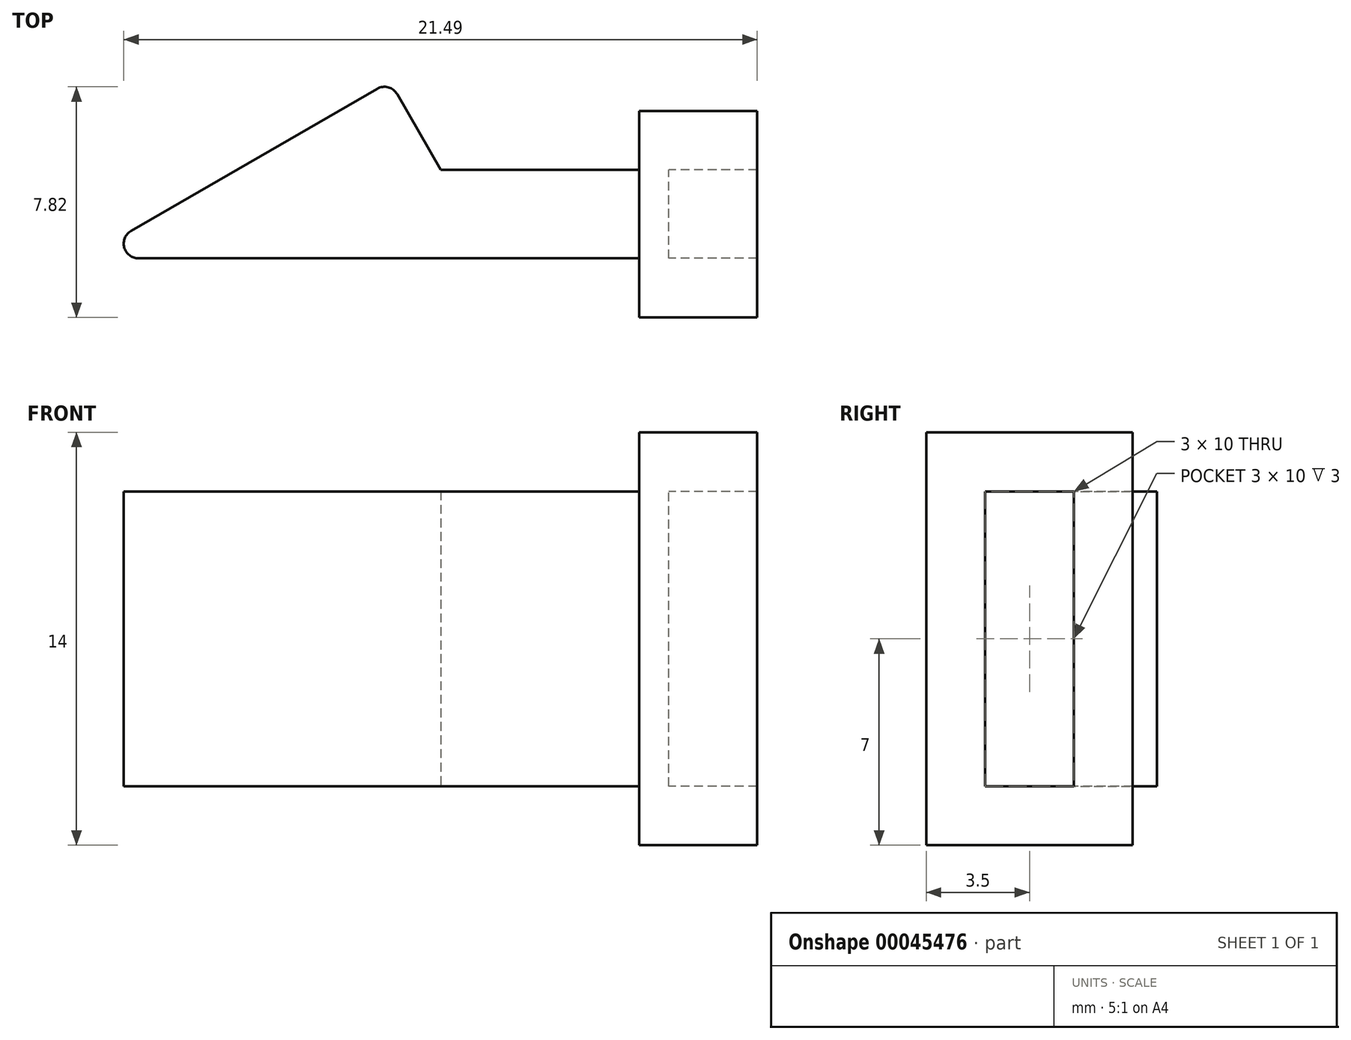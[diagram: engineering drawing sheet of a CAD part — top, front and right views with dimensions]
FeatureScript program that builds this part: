
annotation { "Feature Type Name" : "Feature", "Feature Type Description" : "" }
export const myFeature = defineFeature(function(context is Context, id is Id, definition is map)
    precondition{}
    {
        {
            var Q0;
            Q0=qCreatedBy(makeId("Top.planeOp"),FACE);
            var sketch = newSketch(context, id + "F0", { "sketchPlane" : qUnion([Q0])});
            skLineSegment(sketch, "E0", {"start": v(0, 0) * mm, "end": v(-13.86, 0) * mm});
            skLineSegment(sketch, "E1", {"start": v(-13.86, 0) * mm, "end": v(-3.46, 6) * mm});
            skLineSegment(sketch, "E2", {"start": v(-3.46, 6) * mm, "end": v(0, 0) * mm});
            skLineSegment(sketch, "E3", {"start": v(-3.46, 6) * mm, "end": v(-3.46, 0) * mm, "construction": true});
            skSolve(sketch);
        }
        {
            var Q0;
            Q0=qSketchRegion(id+"F0",true);
            extrude(context, id + "F1", {"entities" : qUnion([Q0]), "depth" : 10 * mm});
        }
        {
            var Q0;
            Q0=qCreatedBy(makeId("Right.planeOp"),FACE);
            cPlane(context, id + "F2", {"entities" : qUnion([Q0]), "cplaneType" : CPlaneType.OFFSET, "offset" : 3.46 * mm, "oppositeDirection" : true, "width" : 150 * mm, "height" : 150 * mm});
        }
        {
            var Q0;
            Q0=qCreatedBy(id+"F2.planeOp",FACE);
            var sketch = newSketch(context, id + "F3", { "sketchPlane" : qUnion([Q0])});
            skLineSegment(sketch, "E4.bottom", {"start": v(0, 0) * mm, "end": v(3, 0) * mm});
            skLineSegment(sketch, "E4.top", {"start": v(0, 10) * mm, "end": v(3, 10) * mm});
            skLineSegment(sketch, "E4.left", {"start": v(0, 0) * mm, "end": v(0, 10) * mm});
            skLineSegment(sketch, "E4.right", {"start": v(3, 0) * mm, "end": v(3, 10) * mm});
            skSolve(sketch);
        }
        {
            var Q0;
            Q0=qSketchRegion(id+"F3",true);
            extrude(context, id + "F4", {"entities" : qUnion([Q0]), "operationType" : NewBodyOperationType.ADD, "depth" : 9.46 * mm});
        }
        {
            var Q0;
            Q0=makeQuery(id+"F4.opExtrude","CAP_FACE",FACE,{"disambiguationData":[OSD([sQuery(id+"F3.wireOp",EDGE,"E4.bottom"),sQuery(id+"F3.wireOp",EDGE,"E4.top"),sQuery(id+"F3.wireOp",EDGE,"E4.left"),sQuery(id+"F3.wireOp",EDGE,"E4.right")])],"isStart":false});
            var sketch = newSketch(context, id + "F5", { "sketchPlane" : qUnion([Q0])});
            skLineSegment(sketch, "E5.bottom", {"start": v(-2, 12) * mm, "end": v(5, 12) * mm});
            skLineSegment(sketch, "E5.top", {"start": v(-2, -2) * mm, "end": v(5, -2) * mm});
            skLineSegment(sketch, "E5.left", {"start": v(-2, 12) * mm, "end": v(-2, -2) * mm});
            skLineSegment(sketch, "E5.right", {"start": v(5, 12) * mm, "end": v(5, -2) * mm});
            skLineSegment(sketch, "E6.bottom", {"start": v(0, 10) * mm, "end": v(3, 10) * mm});
            skLineSegment(sketch, "E6.top", {"start": v(0, 0) * mm, "end": v(3, 0) * mm});
            skLineSegment(sketch, "E6.left", {"start": v(0, 10) * mm, "end": v(0, 0) * mm});
            skLineSegment(sketch, "E6.right", {"start": v(3, 10) * mm, "end": v(3, 0) * mm});
            skSolve(sketch);
        }
        {
            var Q0;
            Q0=makeQuery(id+"F5.imprint","IMPRINT",FACE,{"disambiguationData":[TD([[makeQuery(id+"F5.imprint","IMPRINT",EDGE,{"derivedFrom":sQuery(id+"F5.wireOp",EDGE,"E5.bottom")}),-1.0]])]});
            extrude(context, id + "F6", {"entities" : qUnion([Q0]), "operationType" : NewBodyOperationType.ADD, "depth" : 3 * mm, "hasSecondDirection" : true, "secondDirectionOppositeDirection" : true, "secondDirectionDepth" : 1 * mm});
        }
        {
            var Q0;
            Q0=makeQuery(id+"F1.opExtrude","SWEPT_EDGE",EDGE,{"disambiguationData":[OSD([sQuery(id+"F0.wireOp",EDGE,"E0"),sQuery(id+"F0.wireOp",EDGE,"E1")])]});
            var Q1;
            Q1=makeQuery(id+"F1.opExtrude","SWEPT_EDGE",EDGE,{"disambiguationData":[OSD([sQuery(id+"F0.wireOp",EDGE,"E1"),sQuery(id+"F0.wireOp",EDGE,"E2")])]});
            fillet(context, id + "F7", {"entities" : qUnion([Q0, Q1]), "radius" : 0.5 * mm, "tangentPropagation" : true, "allowEdgeOverflow" : false});
        }
    });
